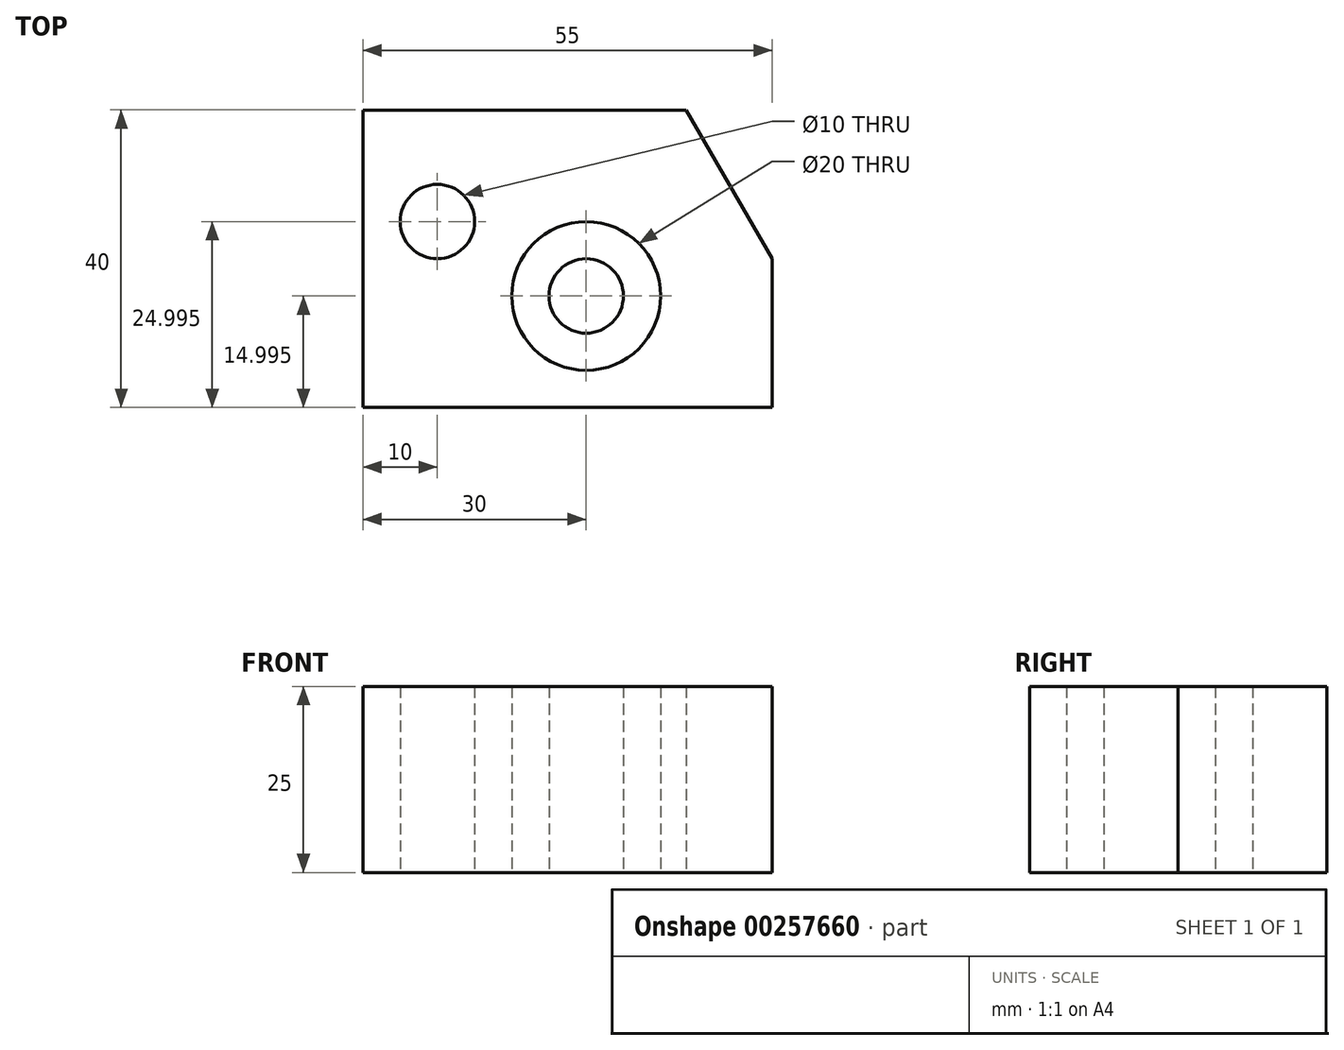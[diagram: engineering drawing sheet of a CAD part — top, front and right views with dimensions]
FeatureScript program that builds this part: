
annotation { "Feature Type Name" : "Feature", "Feature Type Description" : "" }
export const myFeature = defineFeature(function(context is Context, id is Id, definition is map)
    precondition{}
    {
        {
            var Q0;
            Q0=qCreatedBy(makeId("Top.planeOp"),FACE);
            var sketch = newSketch(context, id + "F0", { "sketchPlane" : qUnion([Q0])});
            skLineSegment(sketch, "E0", {"start": v(-37.62, -36.03) * mm, "end": v(17.38, -36.03) * mm});
            skLineSegment(sketch, "E1", {"start": v(-37.62, -36.03) * mm, "end": v(-37.62, 3.97) * mm});
            skLineSegment(sketch, "E2", {"start": v(17.38, -36.03) * mm, "end": v(17.38, -16.03) * mm});
            skLineSegment(sketch, "E3", {"start": v(17.38, -16.03) * mm, "end": v(5.83, 3.97) * mm});
            skLineSegment(sketch, "E4", {"start": v(5.83, 3.97) * mm, "end": v(-37.62, 3.97) * mm});
            skCircle(sketch, "E5", {"center": v(-27.62, -11.03) * mm, "radius": 5 * mm});
            skCircle(sketch, "E6", {"center": v(-7.62, -21.03) * mm, "radius": 5 * mm});
            skCircle(sketch, "E7", {"center": v(-7.62, -21.03) * mm, "radius": 10 * mm});
            skSolve(sketch);
        }
        {
            var Q0;
            Q0 = qSketchRegion(id + "F0", true);
            var Q1;
            Q1=makeQuery(id+"F0.imprint","IMPRINT",FACE,{"disambiguationData":[TD([[makeQuery(id+"F0.imprint","IMPRINT",EDGE,{"derivedFrom":sQuery(id+"F0.wireOp",EDGE,"E6")}),1.0]])]});
            extrude(context, id + "F1", {"entities" : qUnion([Q0, Q1]), "depth" : 25 * mm});
        }
    });
